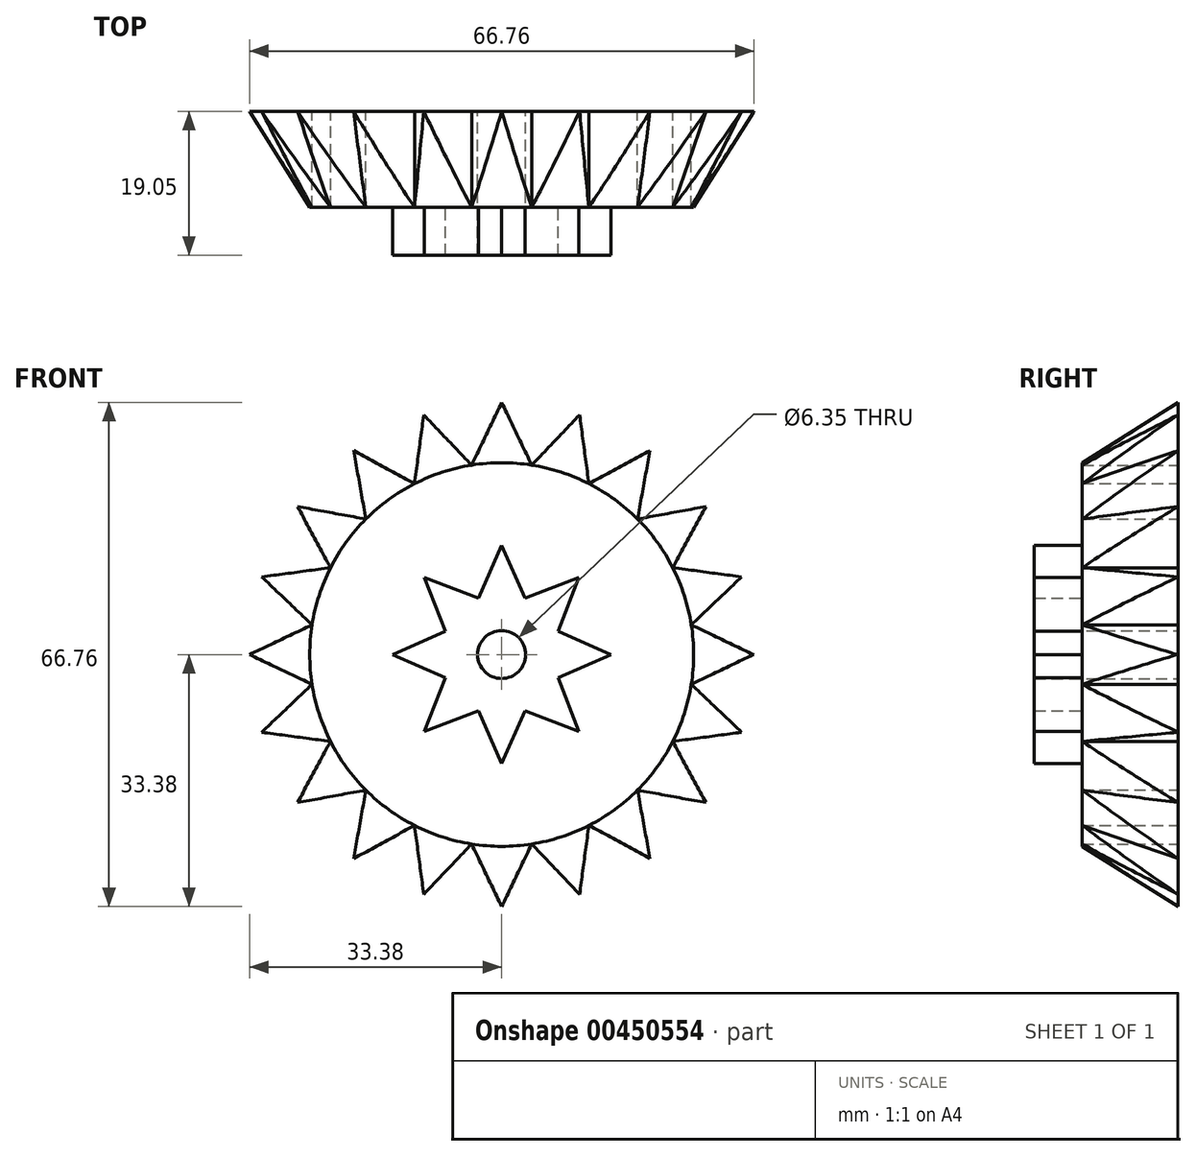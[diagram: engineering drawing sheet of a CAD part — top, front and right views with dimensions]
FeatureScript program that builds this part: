
annotation { "Feature Type Name" : "Feature", "Feature Type Description" : "" }
export const myFeature = defineFeature(function(context is Context, id is Id, definition is map)
    precondition{}
    {
        {
            var Q0;
            Q0=qCreatedBy(makeId("Front.planeOp"),FACE);
            var sketch = newSketch(context, id + "F0", { "sketchPlane" : qUnion([Q0])});
            skCircle(sketch, "E0", {"center": v(0, 0) * mm, "radius": 25.4 * mm});
            skPoint(sketch, "E1", {"position": v(0, 25.4) * mm});
            skPoint(sketch, "E2", {"position": v(3.98, 25.09) * mm});
            skPoint(sketch, "E3", {"position": v(7.86, 24.15) * mm});
            skPoint(sketch, "E4", {"position": v(11.54, 22.63) * mm});
            skPoint(sketch, "E5", {"position": v(14.94, 20.54) * mm});
            skPoint(sketch, "E6", {"position": v(17.98, 17.95) * mm});
            skPoint(sketch, "E7", {"position": v(20.56, 14.9) * mm});
            skPoint(sketch, "E8", {"position": v(22.64, 11.5) * mm});
            skPoint(sketch, "E9", {"position": v(24.17, 7.82) * mm});
            skPoint(sketch, "E10", {"position": v(25.1, 3.94) * mm});
            skPoint(sketch, "E11", {"position": v(25.4, -0.04) * mm});
            skPoint(sketch, "E12", {"position": v(25.08, -4.02) * mm});
            skPoint(sketch, "E13", {"position": v(24.14, -7.9) * mm});
            skPoint(sketch, "E14", {"position": v(22.6, -11.58) * mm});
            skPoint(sketch, "E15", {"position": v(20.52, -14.98) * mm});
            skPoint(sketch, "E16", {"position": v(17.92, -18) * mm});
            skPoint(sketch, "E17", {"position": v(14.88, -20.59) * mm});
            skPoint(sketch, "E18", {"position": v(11.47, -22.66) * mm});
            skPoint(sketch, "E19", {"position": v(7.78, -24.18) * mm});
            skPoint(sketch, "E20", {"position": v(3.9, -25.1) * mm});
            skPoint(sketch, "E21", {"position": v(-0.08, -25.4) * mm});
            skPoint(sketch, "E22.MirrorP", {"position": v(-3.98, 25.09) * mm});
            skPoint(sketch, "E23.MirrorP", {"position": v(-7.86, 24.15) * mm});
            skPoint(sketch, "E24.MirrorP", {"position": v(-11.54, 22.63) * mm});
            skPoint(sketch, "E25.MirrorP", {"position": v(-14.94, 20.54) * mm});
            skPoint(sketch, "E26.MirrorP", {"position": v(-17.98, 17.95) * mm});
            skPoint(sketch, "E27.MirrorP", {"position": v(-20.56, 14.9) * mm});
            skPoint(sketch, "E28.MirrorP", {"position": v(-22.64, 11.5) * mm});
            skPoint(sketch, "E29.MirrorP", {"position": v(-24.17, 7.82) * mm});
            skPoint(sketch, "E30.MirrorP", {"position": v(-25.1, 3.94) * mm});
            skPoint(sketch, "E31.MirrorP", {"position": v(-25.4, -0.04) * mm});
            skPoint(sketch, "E32.MirrorP", {"position": v(-25.08, -4.02) * mm});
            skPoint(sketch, "E33.MirrorP", {"position": v(-24.14, -7.9) * mm});
            skPoint(sketch, "E34.MirrorP", {"position": v(-22.6, -11.58) * mm});
            skPoint(sketch, "E35.MirrorP", {"position": v(-20.52, -14.98) * mm});
            skPoint(sketch, "E36.MirrorP", {"position": v(-17.92, -18) * mm});
            skPoint(sketch, "E37.MirrorP", {"position": v(-14.88, -20.59) * mm});
            skPoint(sketch, "E38.MirrorP", {"position": v(-11.47, -22.66) * mm});
            skPoint(sketch, "E39.MirrorP", {"position": v(-7.78, -24.18) * mm});
            skPoint(sketch, "E40.MirrorP", {"position": v(-3.9, -25.1) * mm});
            skLineSegment(sketch, "E41", {"start": v(0, 25.4) * mm, "end": v(-0.08, -25.4) * mm});
            skLineSegment(sketch, "E42", {"start": v(7.86, 24.15) * mm, "end": v(-7.78, -24.18) * mm});
            skLineSegment(sketch, "E43", {"start": v(14.94, 20.54) * mm, "end": v(-14.88, -20.59) * mm});
            skLineSegment(sketch, "E44", {"start": v(20.56, 14.9) * mm, "end": v(-20.52, -14.98) * mm});
            skLineSegment(sketch, "E45", {"start": v(24.17, 7.82) * mm, "end": v(-24.14, -7.9) * mm});
            skLineSegment(sketch, "E46", {"start": v(-25.4, -0.04) * mm, "end": v(25.4, -0.04) * mm});
            skLineSegment(sketch, "E47", {"start": v(24.14, -7.9) * mm, "end": v(-24.17, 7.82) * mm});
            skLineSegment(sketch, "E48", {"start": v(-20.56, 14.9) * mm, "end": v(20.52, -14.98) * mm});
            skLineSegment(sketch, "E49", {"start": v(14.88, -20.59) * mm, "end": v(-14.94, 20.54) * mm});
            skLineSegment(sketch, "E50", {"start": v(-7.86, 24.15) * mm, "end": v(7.78, -24.18) * mm});
            skLineSegment(sketch, "E51", {"start": v(0, 25.4) * mm, "end": v(0, 33.38) * mm});
            skLineSegment(sketch, "E52", {"start": v(0, 33.38) * mm, "end": v(3.98, 25.09) * mm});
            skLineSegment(sketch, "E53", {"start": v(7.86, 24.15) * mm, "end": v(10.31, 31.75) * mm});
            skLineSegment(sketch, "E54", {"start": v(-7.86, 24.15) * mm, "end": v(-10.31, 31.75) * mm});
            skLineSegment(sketch, "E55", {"start": v(-20.56, 14.9) * mm, "end": v(-27.02, 19.6) * mm});
            skLineSegment(sketch, "E56", {"start": v(-24.17, 7.82) * mm, "end": v(-31.76, 10.29) * mm});
            skLineSegment(sketch, "E57", {"start": v(14.94, 20.54) * mm, "end": v(19.63, 27) * mm});
            skLineSegment(sketch, "E58", {"start": v(20.56, 14.9) * mm, "end": v(27.02, 19.6) * mm});
            skLineSegment(sketch, "E59", {"start": v(24.17, 7.82) * mm, "end": v(31.76, 10.29) * mm});
            skLineSegment(sketch, "E60", {"start": v(25.4, -0.04) * mm, "end": v(33.38, -0.04) * mm});
            skLineSegment(sketch, "E61", {"start": v(-25.4, -0.04) * mm, "end": v(-33.38, 0) * mm});
            skLineSegment(sketch, "E62", {"start": v(-14.94, 20.54) * mm, "end": v(-19.6, 27.02) * mm});
            skLineSegment(sketch, "E63", {"start": v(0, 33.38) * mm, "end": v(-3.98, 25.09) * mm});
            skLineSegment(sketch, "E64", {"start": v(-3.98, 25.09) * mm, "end": v(-10.31, 31.75) * mm});
            skLineSegment(sketch, "E65", {"start": v(-10.31, 31.75) * mm, "end": v(-11.54, 22.63) * mm});
            skLineSegment(sketch, "E66", {"start": v(-11.54, 22.63) * mm, "end": v(-19.6, 27.02) * mm});
            skLineSegment(sketch, "E67", {"start": v(-19.6, 27.02) * mm, "end": v(-17.98, 17.95) * mm});
            skLineSegment(sketch, "E68", {"start": v(-17.98, 17.95) * mm, "end": v(-27.02, 19.6) * mm});
            skLineSegment(sketch, "E69", {"start": v(-27.02, 19.6) * mm, "end": v(-22.64, 11.5) * mm});
            skLineSegment(sketch, "E70", {"start": v(-22.64, 11.5) * mm, "end": v(-31.76, 10.29) * mm});
            skLineSegment(sketch, "E71", {"start": v(-31.76, 10.29) * mm, "end": v(-25.1, 3.94) * mm});
            skLineSegment(sketch, "E72", {"start": v(-25.1, 3.94) * mm, "end": v(-33.38, 0) * mm});
            skLineSegment(sketch, "E73", {"start": v(33.38, -0.04) * mm, "end": v(25.1, 3.94) * mm});
            skLineSegment(sketch, "E74", {"start": v(25.1, 3.94) * mm, "end": v(31.76, 10.29) * mm});
            skLineSegment(sketch, "E75", {"start": v(31.76, 10.29) * mm, "end": v(22.64, 11.5) * mm});
            skLineSegment(sketch, "E76", {"start": v(22.64, 11.5) * mm, "end": v(27.02, 19.6) * mm});
            skLineSegment(sketch, "E77", {"start": v(27.02, 19.6) * mm, "end": v(17.98, 17.95) * mm});
            skLineSegment(sketch, "E78", {"start": v(17.98, 17.95) * mm, "end": v(19.63, 27) * mm});
            skLineSegment(sketch, "E79", {"start": v(19.63, 27) * mm, "end": v(11.54, 22.63) * mm});
            skLineSegment(sketch, "E80", {"start": v(11.54, 22.63) * mm, "end": v(10.31, 31.75) * mm});
            skLineSegment(sketch, "E81", {"start": v(10.31, 31.75) * mm, "end": v(3.98, 25.09) * mm});
            skLineSegment(sketch, "E82.MirrorCS", {"start": v(-25.1, -3.94) * mm, "end": v(-33.38, 0) * mm});
            skLineSegment(sketch, "E83.MirrorCS", {"start": v(-31.76, -10.29) * mm, "end": v(-25.1, -3.94) * mm});
            skLineSegment(sketch, "E84.MirrorCS", {"start": v(-22.64, -11.5) * mm, "end": v(-31.76, -10.29) * mm});
            skLineSegment(sketch, "E85.MirrorCS", {"start": v(-27.02, -19.6) * mm, "end": v(-22.64, -11.5) * mm});
            skLineSegment(sketch, "E86.MirrorCS", {"start": v(-17.98, -17.95) * mm, "end": v(-27.02, -19.6) * mm});
            skLineSegment(sketch, "E87.MirrorCS", {"start": v(-19.6, -27.02) * mm, "end": v(-17.98, -17.95) * mm});
            skLineSegment(sketch, "E88.MirrorCS", {"start": v(-11.54, -22.63) * mm, "end": v(-19.6, -27.02) * mm});
            skLineSegment(sketch, "E89.MirrorCS", {"start": v(-10.31, -31.75) * mm, "end": v(-11.54, -22.63) * mm});
            skLineSegment(sketch, "E90.MirrorCS", {"start": v(-3.98, -25.09) * mm, "end": v(-10.31, -31.75) * mm});
            skLineSegment(sketch, "E91.MirrorCS", {"start": v(0, -33.38) * mm, "end": v(-3.98, -25.09) * mm});
            skLineSegment(sketch, "E92.MirrorCS", {"start": v(0, -33.38) * mm, "end": v(3.98, -25.09) * mm});
            skLineSegment(sketch, "E93.MirrorCS", {"start": v(10.31, -31.75) * mm, "end": v(3.98, -25.09) * mm});
            skLineSegment(sketch, "E94.MirrorCS", {"start": v(11.54, -22.63) * mm, "end": v(10.31, -31.75) * mm});
            skLineSegment(sketch, "E95.MirrorCS", {"start": v(19.63, -27) * mm, "end": v(11.54, -22.63) * mm});
            skLineSegment(sketch, "E96.MirrorCS", {"start": v(17.98, -17.95) * mm, "end": v(19.63, -27) * mm});
            skLineSegment(sketch, "E97.MirrorCS", {"start": v(27.02, -19.6) * mm, "end": v(17.98, -17.95) * mm});
            skLineSegment(sketch, "E98.MirrorCS", {"start": v(22.64, -11.5) * mm, "end": v(27.02, -19.6) * mm});
            skLineSegment(sketch, "E99.MirrorCS", {"start": v(31.76, -10.29) * mm, "end": v(22.64, -11.5) * mm});
            skLineSegment(sketch, "E100.MirrorCS", {"start": v(25.1, -3.94) * mm, "end": v(31.76, -10.29) * mm});
            skLineSegment(sketch, "E101.MirrorCS", {"start": v(33.38, 0.04) * mm, "end": v(25.1, -3.94) * mm});
            skSolve(sketch);
        }
        {
            var Q0;
            Q0=qSketchRegion(id+"F0",true);
            extrude(context, id + "F1", {"entities" : qUnion([Q0]), "endBound" : BoundingType.SYMMETRIC, "depth" : 12.7 * mm});
        }
        {
            var Q0;
            Q0=qCreatedBy(makeId("Right.planeOp"),FACE);
            var sketch = newSketch(context, id + "F2", { "sketchPlane" : qUnion([Q0])});
            skLineSegment(sketch, "E102", {"start": v(0, 0) * mm, "end": v(-6.35, 0) * mm});
            skLineSegment(sketch, "E103", {"start": v(-6.35, 0) * mm, "end": v(-6.35, -25.4) * mm});
            skLineSegment(sketch, "E104", {"start": v(0, -33.38) * mm, "end": v(-6.35, -33.38) * mm});
            skLineSegment(sketch, "E105", {"start": v(-6.35, -33.38) * mm, "end": v(-6.35, -25.4) * mm});
            skLineSegment(sketch, "E106", {"start": v(0, -33.38) * mm, "end": v(6.35, -33.38) * mm});
            skLineSegment(sketch, "E107", {"start": v(6.35, -33.38) * mm, "end": v(-6.35, -25.4) * mm});
            skSolve(sketch);
        }
        {
            var Q0;
            Q0=qSketchRegion(id+"F2",true);
            var Q1;
            Q1=sQuery(id+"F2.wireOp",EDGE,"E102");
            revolve(context, id + "F3", {"operationType" : NewBodyOperationType.REMOVE, "entities" : qUnion([Q0]), "axis" : qUnion([Q1]), "revolveType" : RevolveType.FULL, "oppositeDirection" : true});
        }
        {
            var Q0;
            Q0=makeQuery(id+"F1.opExtrude","CAP_FACE",FACE,{"disambiguationData":[OSD([sQuery(id+"F0.wireOp",EDGE,"E41"),sQuery(id+"F0.wireOp",EDGE,"E42"),sQuery(id+"F0.wireOp",EDGE,"E43"),sQuery(id+"F0.wireOp",EDGE,"E44"),sQuery(id+"F0.wireOp",EDGE,"E45"),sQuery(id+"F0.wireOp",EDGE,"E46"),sQuery(id+"F0.wireOp",EDGE,"E47"),sQuery(id+"F0.wireOp",EDGE,"E48"),sQuery(id+"F0.wireOp",EDGE,"E49"),sQuery(id+"F0.wireOp",EDGE,"E50"),sQuery(id+"F0.wireOp",EDGE,"E52"),sQuery(id+"F0.wireOp",EDGE,"E60"),sQuery(id+"F0.wireOp",EDGE,"E63"),sQuery(id+"F0.wireOp",EDGE,"E64"),sQuery(id+"F0.wireOp",EDGE,"E65"),sQuery(id+"F0.wireOp",EDGE,"E66"),sQuery(id+"F0.wireOp",EDGE,"E67"),sQuery(id+"F0.wireOp",EDGE,"E68"),sQuery(id+"F0.wireOp",EDGE,"E69"),sQuery(id+"F0.wireOp",EDGE,"E70"),sQuery(id+"F0.wireOp",EDGE,"E71"),sQuery(id+"F0.wireOp",EDGE,"E72"),sQuery(id+"F0.wireOp",EDGE,"E73"),sQuery(id+"F0.wireOp",EDGE,"E74"),sQuery(id+"F0.wireOp",EDGE,"E75"),sQuery(id+"F0.wireOp",EDGE,"E76"),sQuery(id+"F0.wireOp",EDGE,"E77"),sQuery(id+"F0.wireOp",EDGE,"E78"),sQuery(id+"F0.wireOp",EDGE,"E79"),sQuery(id+"F0.wireOp",EDGE,"E80"),sQuery(id+"F0.wireOp",EDGE,"E81"),sQuery(id+"F0.wireOp",EDGE,"E82.MirrorCS"),sQuery(id+"F0.wireOp",EDGE,"E83.MirrorCS"),sQuery(id+"F0.wireOp",EDGE,"E84.MirrorCS"),sQuery(id+"F0.wireOp",EDGE,"E85.MirrorCS"),sQuery(id+"F0.wireOp",EDGE,"E86.MirrorCS"),sQuery(id+"F0.wireOp",EDGE,"E87.MirrorCS"),sQuery(id+"F0.wireOp",EDGE,"E88.MirrorCS"),sQuery(id+"F0.wireOp",EDGE,"E89.MirrorCS"),sQuery(id+"F0.wireOp",EDGE,"E90.MirrorCS"),sQuery(id+"F0.wireOp",EDGE,"E91.MirrorCS"),sQuery(id+"F0.wireOp",EDGE,"E92.MirrorCS"),sQuery(id+"F0.wireOp",EDGE,"E93.MirrorCS"),sQuery(id+"F0.wireOp",EDGE,"E94.MirrorCS"),sQuery(id+"F0.wireOp",EDGE,"E95.MirrorCS"),sQuery(id+"F0.wireOp",EDGE,"E96.MirrorCS"),sQuery(id+"F0.wireOp",EDGE,"E97.MirrorCS"),sQuery(id+"F0.wireOp",EDGE,"E98.MirrorCS"),sQuery(id+"F0.wireOp",EDGE,"E99.MirrorCS"),sQuery(id+"F0.wireOp",EDGE,"E100.MirrorCS"),sQuery(id+"F0.wireOp",EDGE,"E101.MirrorCS")])],"isStart":false});
            var sketch = newSketch(context, id + "F4", { "sketchPlane" : qUnion([Q0])});
            skCircle(sketch, "E108", {"center": v(0, 0) * mm, "radius": 8.09 * mm});
            skPoint(sketch, "E109", {"position": v(0, 8.09) * mm});
            skPoint(sketch, "E110.1.0", {"position": v(3.1, 7.47) * mm});
            skPoint(sketch, "E110.2.0", {"position": v(5.72, 5.72) * mm});
            skPoint(sketch, "E110.3.0", {"position": v(7.47, 3.1) * mm});
            skPoint(sketch, "E110.4.0", {"position": v(8.09, 0) * mm});
            skPoint(sketch, "E110.5.0", {"position": v(7.47, -3.1) * mm});
            skPoint(sketch, "E110.6.0", {"position": v(5.72, -5.72) * mm});
            skLineSegment(sketch, "E110.anchor1", {"start": v(0, 0) * mm, "end": v(0, 8.09) * mm, "construction": true});
            skLineSegment(sketch, "E110.anchor2", {"start": v(0, 0) * mm, "end": v(3.1, -7.47) * mm, "construction": true});
            skPoint(sketch, "E111.0.7.0", {"position": v(3.1, -7.47) * mm});
            skPoint(sketch, "E112", {"position": v(0, -8.09) * mm});
            skPoint(sketch, "E113.1.0", {"position": v(-3.1, -7.47) * mm});
            skPoint(sketch, "E113.2.0", {"position": v(-5.72, -5.72) * mm});
            skPoint(sketch, "E113.3.0", {"position": v(-7.47, -3.1) * mm});
            skPoint(sketch, "E113.4.0", {"position": v(-8.09, 0) * mm});
            skPoint(sketch, "E113.5.0", {"position": v(-7.47, 3.1) * mm});
            skPoint(sketch, "E113.6.0", {"position": v(-5.72, 5.72) * mm});
            skPoint(sketch, "E113.7.0", {"position": v(-3.1, 7.47) * mm});
            skLineSegment(sketch, "E113.anchor1", {"start": v(0, 0) * mm, "end": v(0, -8.09) * mm, "construction": true});
            skLineSegment(sketch, "E113.anchor2", {"start": v(0, 0) * mm, "end": v(-3.1, 7.47) * mm, "construction": true});
            skLineSegment(sketch, "E114", {"start": v(0, 8.09) * mm, "end": v(0, 14.44) * mm});
            skLineSegment(sketch, "E115", {"start": v(0, 0) * mm, "end": v(3.1, 7.47) * mm});
            skLineSegment(sketch, "E116", {"start": v(0, 0) * mm, "end": v(5.72, 5.72) * mm});
            skLineSegment(sketch, "E117", {"start": v(0, 0) * mm, "end": v(7.47, 3.1) * mm});
            skLineSegment(sketch, "E118", {"start": v(0, 0) * mm, "end": v(8.09, 0) * mm});
            skLineSegment(sketch, "E119", {"start": v(0, 0) * mm, "end": v(7.47, -3.1) * mm});
            skLineSegment(sketch, "E120", {"start": v(0, 0) * mm, "end": v(5.72, -5.72) * mm});
            skLineSegment(sketch, "E121", {"start": v(0, 0) * mm, "end": v(3.1, -7.47) * mm});
            skLineSegment(sketch, "E122", {"start": v(0, 0) * mm, "end": v(-3.1, -7.47) * mm});
            skLineSegment(sketch, "E123", {"start": v(0, 0) * mm, "end": v(-5.72, -5.72) * mm});
            skLineSegment(sketch, "E124", {"start": v(0, 0) * mm, "end": v(-7.47, -3.1) * mm});
            skLineSegment(sketch, "E125", {"start": v(0, 0) * mm, "end": v(-7.47, 3.1) * mm});
            skLineSegment(sketch, "E126", {"start": v(0, 0) * mm, "end": v(-5.72, 5.72) * mm});
            skLineSegment(sketch, "E127", {"start": v(0, 0) * mm, "end": v(-3.1, 7.47) * mm});
            skLineSegment(sketch, "E128", {"start": v(5.72, 5.72) * mm, "end": v(10.2, 10.2) * mm});
            skLineSegment(sketch, "E129", {"start": v(8.09, 0) * mm, "end": v(14.44, 0) * mm});
            skLineSegment(sketch, "E130", {"start": v(5.72, -5.72) * mm, "end": v(10.2, -10.2) * mm});
            skLineSegment(sketch, "E131", {"start": v(0, -8.09) * mm, "end": v(0, -14.44) * mm});
            skLineSegment(sketch, "E132", {"start": v(-5.72, -5.72) * mm, "end": v(-10.2, -10.2) * mm});
            skLineSegment(sketch, "E133", {"start": v(-8.09, 0) * mm, "end": v(-14.44, 0) * mm});
            skLineSegment(sketch, "E134", {"start": v(-5.72, 5.72) * mm, "end": v(-10.2, 10.2) * mm});
            skLineSegment(sketch, "E135", {"start": v(0, 14.44) * mm, "end": v(-3.1, 7.47) * mm});
            skLineSegment(sketch, "E136", {"start": v(-3.1, 7.47) * mm, "end": v(-10.2, 10.2) * mm});
            skLineSegment(sketch, "E137", {"start": v(-10.2, 10.2) * mm, "end": v(-7.47, 3.1) * mm});
            skLineSegment(sketch, "E138", {"start": v(-7.47, 3.1) * mm, "end": v(-14.44, 0) * mm});
            skLineSegment(sketch, "E139", {"start": v(-14.44, 0) * mm, "end": v(-7.47, -3.1) * mm});
            skLineSegment(sketch, "E140", {"start": v(-7.47, -3.1) * mm, "end": v(-10.2, -10.2) * mm});
            skLineSegment(sketch, "E141", {"start": v(-10.2, -10.2) * mm, "end": v(-3.1, -7.47) * mm});
            skLineSegment(sketch, "E142", {"start": v(-3.1, -7.47) * mm, "end": v(0, -14.44) * mm});
            skLineSegment(sketch, "E143", {"start": v(0, -14.44) * mm, "end": v(3.1, -7.47) * mm});
            skLineSegment(sketch, "E144", {"start": v(3.1, -7.47) * mm, "end": v(10.2, -10.2) * mm});
            skLineSegment(sketch, "E145", {"start": v(10.2, -10.2) * mm, "end": v(7.47, -3.1) * mm});
            skLineSegment(sketch, "E146", {"start": v(7.47, -3.1) * mm, "end": v(14.44, 0) * mm});
            skLineSegment(sketch, "E147", {"start": v(14.44, 0) * mm, "end": v(7.47, 3.1) * mm});
            skLineSegment(sketch, "E148", {"start": v(7.47, 3.1) * mm, "end": v(10.2, 10.2) * mm});
            skLineSegment(sketch, "E149", {"start": v(10.2, 10.2) * mm, "end": v(3.1, 7.47) * mm});
            skLineSegment(sketch, "E150", {"start": v(3.1, 7.47) * mm, "end": v(0, 14.44) * mm});
            skSolve(sketch);
        }
        {
            var Q0;
            Q0=qCreatedBy(makeId("Front.planeOp"),FACE);
            var sketch = newSketch(context, id + "F5", { "sketchPlane" : qUnion([Q0])});
            skCircle(sketch, "E151", {"center": v(0, 0) * mm, "radius": 3.17 * mm});
            skSolve(sketch);
        }
        {
            var Q0;
            Q0=qSketchRegion(id+"F4",true);
            extrude(context, id + "F6", {"entities" : qUnion([Q0]), "operationType" : NewBodyOperationType.ADD, "depth" : 6.35 * mm});
        }
        {
            var Q0;
            Q0=qSketchRegion(id+"F5",true);
            extrude(context, id + "F7", {"entities" : qUnion([Q0]), "operationType" : NewBodyOperationType.REMOVE, "endBound" : BoundingType.SYMMETRIC, "depth" : -127 * mm});
        }
    });
